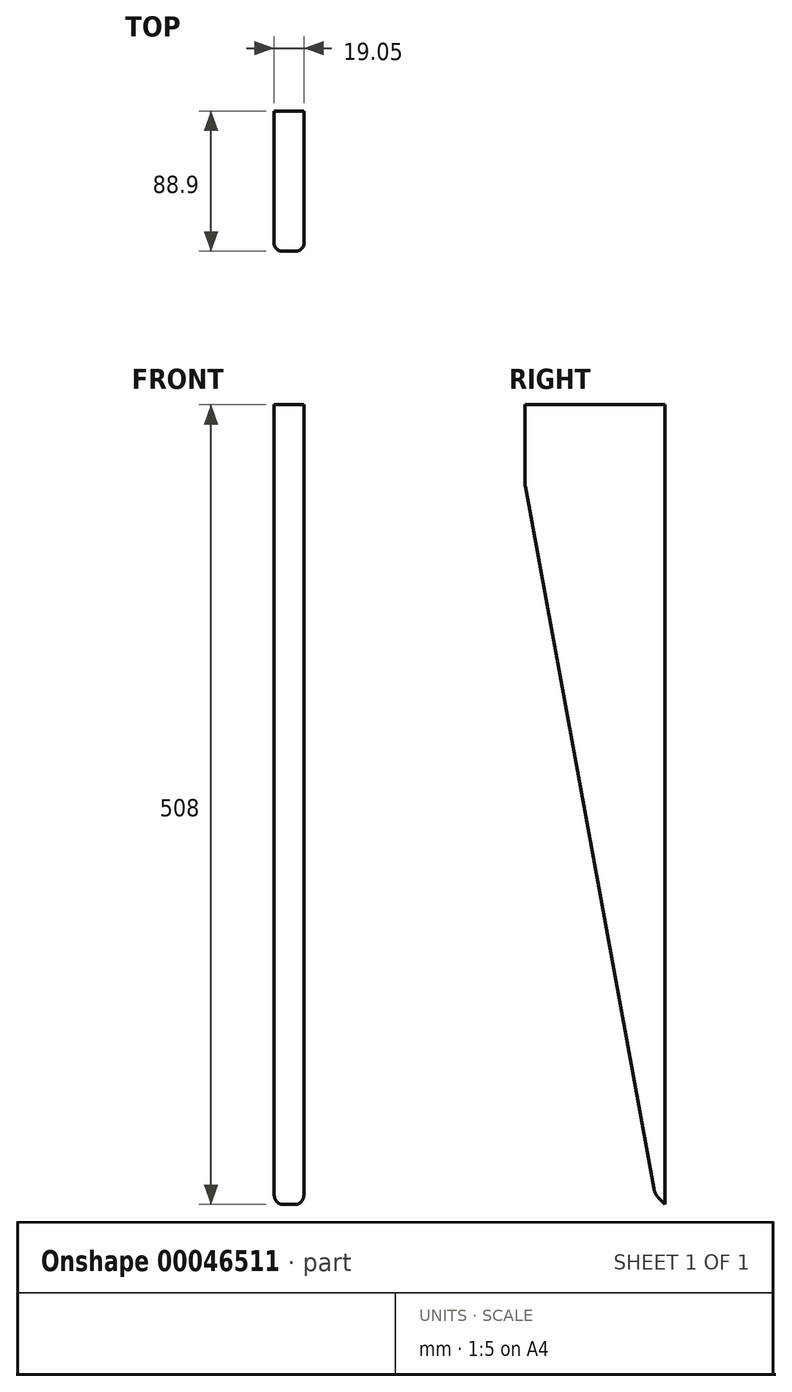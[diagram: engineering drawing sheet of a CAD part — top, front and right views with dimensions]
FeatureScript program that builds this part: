
annotation { "Feature Type Name" : "Feature", "Feature Type Description" : "" }
export const myFeature = defineFeature(function(context is Context, id is Id, definition is map)
    precondition{}
    {
        {
            var Q0;
            Q0=qCreatedBy(makeId("Right.planeOp"),FACE);
            var sketch = newSketch(context, id + "F0", { "sketchPlane" : qUnion([Q0])});
            skLineSegment(sketch, "E0", {"start": v(42.43, 329.25) * mm, "end": v(-46.47, 329.25) * mm});
            skLineSegment(sketch, "E1", {"start": v(-46.47, 329.25) * mm, "end": v(-46.47, 279.6) * mm});
            skLineSegment(sketch, "E2", {"start": v(-46.26, 277.32) * mm, "end": v(35.37, -168.5) * mm});
            skLineSegment(sketch, "E3", {"start": v(38.88, -175.2) * mm, "end": v(42.43, -178.75) * mm});
            skLineSegment(sketch, "E4", {"start": v(42.43, -178.75) * mm, "end": v(42.43, 329.25) * mm});
            skPoint(sketch, "E5.visualSharp", {"position": v(-46.47, 278.45) * mm});
            skArc(sketch, "E5.filletArc", {"start": v(-46.47, 279.6) * mm, "mid": v(-46.42, 278.45) * mm, "end": v(-46.26, 277.32) * mm});
            skPoint(sketch, "E6.visualSharp", {"position": v(36.08, -172.4) * mm});
            skArc(sketch, "E6.filletArc", {"start": v(35.37, -168.5) * mm, "mid": v(36.61, -172.12) * mm, "end": v(38.88, -175.2) * mm});
            skSolve(sketch);
        }
        {
            var Q0;
            Q0=makeQuery(id+"F0.imprint","IMPRINT",FACE,{"disambiguationData":[TD([[makeQuery(id+"F0.imprint","IMPRINT",EDGE,{"derivedFrom":sQuery(id+"F0.wireOp",EDGE,"E0")}),1.0]])]});
            extrude(context, id + "F1", {"entities" : qUnion([Q0]), "depth" : 19.05 * mm});
        }
        {
            var Q0;
            Q0=makeQuery(id+"F1.opExtrude","CAP_EDGE",EDGE,{"disambiguationData":[OSD([sQuery(id+"F0.wireOp",EDGE,"E2")])],"isStart":false});
            var Q1;
            Q1=makeQuery(id+"F1.opExtrude","CAP_EDGE",EDGE,{"disambiguationData":[OSD([sQuery(id+"F0.wireOp",EDGE,"E2")])],"isStart":true});
            fillet(context, id + "F2", {"entities" : qUnion([Q0, Q1]), "radius" : 5.08 * mm, "tangentPropagation" : true, "allowEdgeOverflow" : false});
        }
    });
